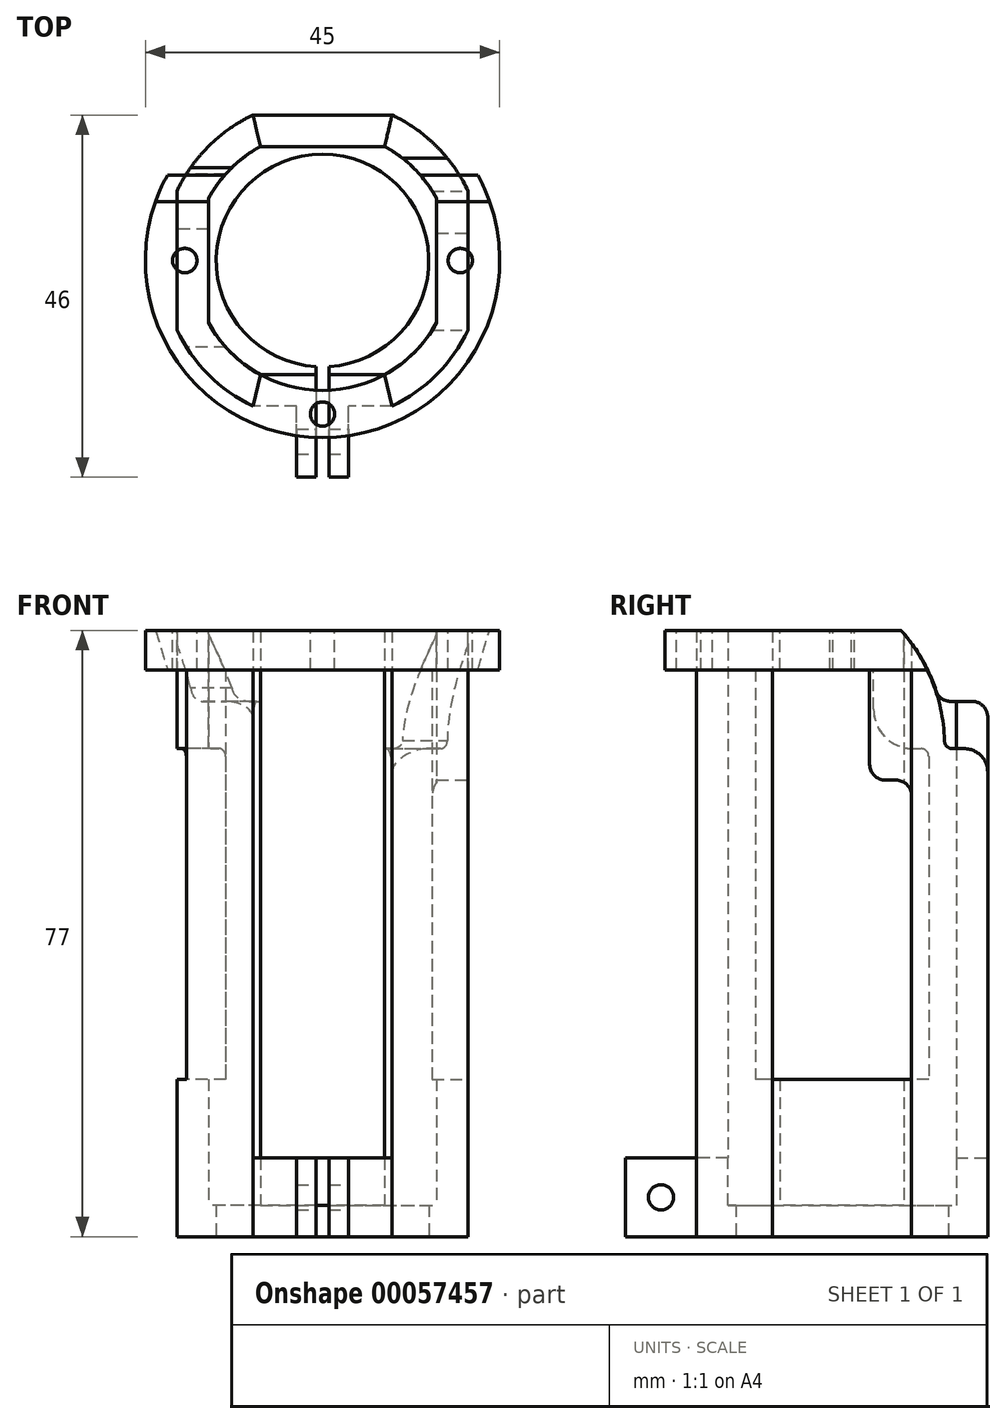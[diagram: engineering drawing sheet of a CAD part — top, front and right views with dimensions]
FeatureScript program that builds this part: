
annotation { "Feature Type Name" : "Feature", "Feature Type Description" : "" }
export const myFeature = defineFeature(function(context is Context, id is Id, definition is map)
    precondition{}
    {
        {
            var Q0;
            Q0=qCreatedBy(makeId("Top.planeOp"),FACE);
            var sketch = newSketch(context, id + "F0", { "sketchPlane" : qUnion([Q0])});
            skArc(sketch, "E0", {"start": v(-7.87, 14.5) * mm, "mid": v(-11.67, 11.67) * mm, "end": v(-14.5, 7.87) * mm});
            skArc(sketch, "E1", {"start": v(-8.83, 18.5) * mm, "mid": v(-14.5, 14.5) * mm, "end": v(-18.5, 8.83) * mm});
            skLineSegment(sketch, "E2.trimOffspring", {"start": v(-7.87, 14.5) * mm, "end": v(7.87, 14.5) * mm});
            skLineSegment(sketch, "E3.1.0", {"start": v(-14.5, -7.87) * mm, "end": v(-14.5, 7.87) * mm});
            skLineSegment(sketch, "E3.2.0", {"start": v(7.87, -14.5) * mm, "end": v(-7.87, -14.5) * mm});
            skLineSegment(sketch, "E3.3.0", {"start": v(14.5, 7.87) * mm, "end": v(14.5, -7.87) * mm});
            skArc(sketch, "E4.trimOffspring", {"start": v(-14.5, -7.87) * mm, "mid": v(-11.67, -11.67) * mm, "end": v(-7.87, -14.5) * mm});
            skArc(sketch, "E5.trimOffspring", {"start": v(14.5, 7.87) * mm, "mid": v(11.67, 11.67) * mm, "end": v(7.87, 14.5) * mm});
            skArc(sketch, "E6.trimOffspring", {"start": v(7.87, -14.5) * mm, "mid": v(11.67, -11.67) * mm, "end": v(14.5, -7.87) * mm});
            skLineSegment(sketch, "E7.0", {"start": v(-8.83, 18.5) * mm, "end": v(8.83, 18.5) * mm});
            skLineSegment(sketch, "E8.1.0", {"start": v(-18.5, -8.83) * mm, "end": v(-18.5, 8.83) * mm});
            skLineSegment(sketch, "E8.2.0", {"start": v(8.83, -18.5) * mm, "end": v(-8.83, -18.5) * mm});
            skLineSegment(sketch, "E8.3.0", {"start": v(18.5, 8.83) * mm, "end": v(18.5, -8.83) * mm});
            skArc(sketch, "E9.trimOffspring", {"start": v(8.83, -18.5) * mm, "mid": v(14.5, -14.5) * mm, "end": v(18.5, -8.83) * mm});
            skArc(sketch, "E10.trimOffspring", {"start": v(18.5, 8.83) * mm, "mid": v(14.5, 14.5) * mm, "end": v(8.83, 18.5) * mm});
            skArc(sketch, "E11.trimOffspring", {"start": v(-18.5, -8.83) * mm, "mid": v(-14.5, -14.5) * mm, "end": v(-8.83, -18.5) * mm});
            skSolve(sketch);
        }
        {
            var Q0;
            Q0 = qSketchRegion(id + "F0", true);
            extrude(context, id + "F1", {"entities" : qUnion([Q0]), "depth" : 10 * mm});
        }
        {
            var Q0;
            Q0=makeQuery(id+"F17.boolean.opBoolean","MERGE",FACE,{"derivedFrom":[makeQuery(id+"F1.opExtrude","CAP_FACE",FACE,{"disambiguationData":[OSD([sQuery(id+"F0.wireOp",EDGE,"E0"),sQuery(id+"F0.wireOp",EDGE,"E1"),sQuery(id+"F0.wireOp",EDGE,"E2.trimOffspring"),sQuery(id+"F0.wireOp",EDGE,"E3.1.0"),sQuery(id+"F0.wireOp",EDGE,"E3.2.0"),sQuery(id+"F0.wireOp",EDGE,"E3.3.0"),sQuery(id+"F0.wireOp",EDGE,"E4.trimOffspring"),sQuery(id+"F0.wireOp",EDGE,"E5.trimOffspring"),sQuery(id+"F0.wireOp",EDGE,"E6.trimOffspring"),sQuery(id+"F0.wireOp",EDGE,"E7.0"),sQuery(id+"F0.wireOp",EDGE,"E8.1.0"),sQuery(id+"F0.wireOp",EDGE,"E8.2.0"),sQuery(id+"F0.wireOp",EDGE,"E8.3.0"),sQuery(id+"F0.wireOp",EDGE,"E9.trimOffspring"),sQuery(id+"F0.wireOp",EDGE,"E10.trimOffspring"),sQuery(id+"F0.wireOp",EDGE,"E11.trimOffspring")])],"isStart":false}),makeQuery(id+"F17.opExtrude","SWEPT_FACE",FACE,{"disambiguationData":[OSD([sQuery(id+"F16.wireOp",EDGE,"E91.top")])]}),makeQuery(id+"F17.opExtrude","SWEPT_FACE",FACE,{"disambiguationData":[OSD([sQuery(id+"F16.wireOp",EDGE,"38b2654b-14ed-417b-8ce9-eae6a770c8082.MirrorCS")])]})]});
            var sketch = newSketch(context, id + "F2", { "sketchPlane" : qUnion([Q0])});
            skArc(sketch, "E12", {"start": v(8.83, -18.5) * mm, "mid": v(14.5, -14.5) * mm, "end": v(18.5, -8.83) * mm});
            skArc(sketch, "E13", {"start": v(8.83, 18.5) * mm, "mid": v(14.5, 14.5) * mm, "end": v(18.5, 8.83) * mm});
            skArc(sketch, "E14", {"start": v(14.5, 7.87) * mm, "mid": v(11.67, 11.67) * mm, "end": v(7.87, 14.5) * mm});
            skArc(sketch, "E15", {"start": v(14.5, -7.87) * mm, "mid": v(11.67, -11.67) * mm, "end": v(7.87, -14.5) * mm});
            skLineSegment(sketch, "E16", {"start": v(14.5, 7.87) * mm, "end": v(14.5, -7.87) * mm});
            skLineSegment(sketch, "E17", {"start": v(18.5, -8.83) * mm, "end": v(18.5, 8.83) * mm});
            skArc(sketch, "E18.MirrorCS", {"start": v(-8.83, -18.5) * mm, "mid": v(-14.5, -14.5) * mm, "end": v(-18.5, -8.83) * mm});
            skArc(sketch, "E19.MirrorCS", {"start": v(-14.5, -7.87) * mm, "mid": v(-11.67, -11.67) * mm, "end": v(-7.87, -14.5) * mm});
            skArc(sketch, "E20.MirrorCS", {"start": v(-8.83, 18.5) * mm, "mid": v(-14.5, 14.5) * mm, "end": v(-18.5, 8.83) * mm});
            skLineSegment(sketch, "E21.MirrorCS", {"start": v(-18.5, -8.83) * mm, "end": v(-18.5, 8.83) * mm});
            skLineSegment(sketch, "E22.MirrorCS", {"start": v(-14.5, 7.87) * mm, "end": v(-14.5, -7.87) * mm});
            skArc(sketch, "E23.MirrorCS", {"start": v(-14.5, 7.87) * mm, "mid": v(-11.67, 11.67) * mm, "end": v(-7.87, 14.5) * mm});
            skLineSegment(sketch, "E24", {"start": v(7.87, 14.5) * mm, "end": v(8.83, 18.5) * mm});
            skPoint(sketch, "E25.orphan", {"position": v(7.01, 19.26) * mm});
            skPoint(sketch, "E26.orphan", {"position": v(5.64, 15.5) * mm});
            skLineSegment(sketch, "E27", {"start": v(7.87, -14.5) * mm, "end": v(8.83, -18.5) * mm});
            skPoint(sketch, "E28.MirrorCS.end.orphan", {"position": v(7.01, -19.26) * mm});
            skPoint(sketch, "E28.MirrorCS.start.orphan", {"position": v(5.64, -15.5) * mm});
            skLineSegment(sketch, "E29", {"start": v(-7.87, 14.5) * mm, "end": v(-8.83, 18.5) * mm});
            skLineSegment(sketch, "E30", {"start": v(-7.87, -14.5) * mm, "end": v(-8.83, -18.5) * mm});
            skPoint(sketch, "E31.MirrorCS.start.orphan", {"position": v(-5.64, -15.5) * mm});
            skPoint(sketch, "E32.orphan", {"position": v(-7.01, -19.26) * mm});
            skPoint(sketch, "E33.orphan", {"position": v(-7.01, 19.26) * mm});
            skPoint(sketch, "E34.orphan", {"position": v(-5.64, 15.5) * mm});
            skSolve(sketch);
        }
        {
            var Q0;
            Q0 = qSketchRegion(id + "F2", true);
            extrude(context, id + "F3", {"entities" : qUnion([Q0]), "operationType" : NewBodyOperationType.ADD, "depth" : 67 * mm});
        }
        {
            var Q0;
            Q0=makeQuery(id+"F3.opExtrude","CAP_FACE",FACE,{"disambiguationData":[OSD([sQuery(id+"F2.wireOp",EDGE,"E18.MirrorCS"),sQuery(id+"F2.wireOp",EDGE,"E19.MirrorCS"),sQuery(id+"F2.wireOp",EDGE,"E20.MirrorCS"),sQuery(id+"F2.wireOp",EDGE,"dc69b4cd-8a5e-4500-a1da-573fba75ecb53.MirrorCS"),sQuery(id+"F2.wireOp",EDGE,"E21.MirrorCS"),sQuery(id+"F2.wireOp",EDGE,"E22.MirrorCS"),sQuery(id+"F2.wireOp",EDGE,"E31.MirrorCS"),sQuery(id+"F2.wireOp",EDGE,"E23.MirrorCS")])],"isStart":false});
            var sketch = newSketch(context, id + "F4", { "sketchPlane" : qUnion([Q0])});
            skArc(sketch, "E35", {"start": v(-14.5, -7.87) * mm, "mid": v(0, -16.5) * mm, "end": v(14.5, -7.87) * mm});
            skArc(sketch, "E36.converted", {"start": v(-12.8, 18.5) * mm, "mid": v(0, -22.5) * mm, "end": v(12.8, 18.5) * mm});
            skLineSegment(sketch, "E37", {"start": v(-12.8, 18.5) * mm, "end": v(12.8, 18.5) * mm});
            skLineSegment(sketch, "E38", {"start": v(-14.5, 7.87) * mm, "end": v(-14.5, -7.87) * mm});
            skLineSegment(sketch, "E39.MirrorCS", {"start": v(14.5, 7.87) * mm, "end": v(14.5, -7.87) * mm});
            skArc(sketch, "E40.trimOffspring", {"start": v(14.5, 7.87) * mm, "mid": v(0, 16.5) * mm, "end": v(-14.5, 7.87) * mm});
            skSolve(sketch);
        }
        {
            var Q0;
            Q0 = qSketchRegion(id + "F4", true);
            extrude(context, id + "F5", {"entities" : qUnion([Q0]), "oppositeDirection" : true, "depth" : 5 * mm});
        }
        {
            var Q0;
            Q0=makeQuery(id+"F5.opExtrude","CAP_FACE",FACE,{"disambiguationData":[OSD([sQuery(id+"F4.wireOp",EDGE,"E35"),sQuery(id+"F4.wireOp",EDGE,"E36.converted"),sQuery(id+"F4.wireOp",EDGE,"E37")])],"isStart":true});
            var sketch = newSketch(context, id + "F6", { "sketchPlane" : qUnion([Q0])});
            skCircle(sketch, "E41", {"center": v(0, -19.5) * mm, "radius": 1.55 * mm});
            skCircle(sketch, "E42", {"center": v(17.5, 0) * mm, "radius": 1.55 * mm});
            skCircle(sketch, "E43", {"center": v(-17.5, 0) * mm, "radius": 1.55 * mm});
            skSolve(sketch);
        }
        {
            var Q0;
            Q0 = qSketchRegion(id + "F6", true);
            extrude(context, id + "F7", {"entities" : qUnion([Q0]), "operationType" : NewBodyOperationType.REMOVE, "oppositeDirection" : true, "depth" : 5 * mm});
        }
        {
            var Q0;
            Q0=makeQuery(id+"F17.boolean.opBoolean","MERGE",FACE,{"derivedFrom":[makeQuery(id+"F1.opExtrude","CAP_FACE",FACE,{"disambiguationData":[OSD([sQuery(id+"F0.wireOp",EDGE,"E0"),sQuery(id+"F0.wireOp",EDGE,"E1"),sQuery(id+"F0.wireOp",EDGE,"E2.trimOffspring"),sQuery(id+"F0.wireOp",EDGE,"E3.1.0"),sQuery(id+"F0.wireOp",EDGE,"E3.2.0"),sQuery(id+"F0.wireOp",EDGE,"E3.3.0"),sQuery(id+"F0.wireOp",EDGE,"E4.trimOffspring"),sQuery(id+"F0.wireOp",EDGE,"E5.trimOffspring"),sQuery(id+"F0.wireOp",EDGE,"E6.trimOffspring"),sQuery(id+"F0.wireOp",EDGE,"E7.0"),sQuery(id+"F0.wireOp",EDGE,"E8.1.0"),sQuery(id+"F0.wireOp",EDGE,"E8.2.0"),sQuery(id+"F0.wireOp",EDGE,"E8.3.0"),sQuery(id+"F0.wireOp",EDGE,"E9.trimOffspring"),sQuery(id+"F0.wireOp",EDGE,"E10.trimOffspring"),sQuery(id+"F0.wireOp",EDGE,"E11.trimOffspring")])],"isStart":true}),makeQuery(id+"F17.opExtrude","SWEPT_FACE",FACE,{"disambiguationData":[OSD([sQuery(id+"F16.wireOp",EDGE,"E91.bottom")])]}),makeQuery(id+"F17.opExtrude","SWEPT_FACE",FACE,{"disambiguationData":[OSD([sQuery(id+"F16.wireOp",EDGE,"38b2654b-14ed-417b-8ce9-eae6a770c8083.MirrorCS")])]})]});
            var sketch = newSketch(context, id + "F8", { "sketchPlane" : qUnion([Q0])});
            skLineSegment(sketch, "E44", {"start": v(-14.5, 7.87) * mm, "end": v(-14.5, -7.87) * mm});
            skLineSegment(sketch, "E45", {"start": v(-7.87, -14.5) * mm, "end": v(7.87, -14.5) * mm});
            skLineSegment(sketch, "E46", {"start": v(-7.87, 14.5) * mm, "end": v(7.87, 14.5) * mm});
            skArc(sketch, "E47", {"start": v(-7.87, 14.5) * mm, "mid": v(-11.67, 11.67) * mm, "end": v(-14.5, 7.87) * mm});
            skArc(sketch, "E48.trimOffspring", {"start": v(-14.5, -7.87) * mm, "mid": v(-11.67, -11.67) * mm, "end": v(-7.87, -14.5) * mm});
            skLineSegment(sketch, "E49", {"start": v(14.5, 7.87) * mm, "end": v(14.5, -7.87) * mm});
            skArc(sketch, "E50.trimOffspring", {"start": v(14.5, 7.87) * mm, "mid": v(11.67, 11.67) * mm, "end": v(7.87, 14.5) * mm});
            skArc(sketch, "E51", {"start": v(7.87, -14.5) * mm, "mid": v(11.67, -11.67) * mm, "end": v(14.5, -7.87) * mm});
            skCircle(sketch, "E52", {"center": v(0, 0) * mm, "radius": 13.5 * mm});
            skSolve(sketch);
        }
        {
            var Q0;
            Q0 = qSketchRegion(id + "F8", true);
            extrude(context, id + "F9", {"entities" : qUnion([Q0]), "operationType" : NewBodyOperationType.ADD, "oppositeDirection" : true, "depth" : 4 * mm});
        }
        {
            var Q0;
            Q0=makeQuery(id+"F3.opExtrude","SWEPT_FACE",FACE,{"disambiguationData":[OSD([sQuery(id+"F2.wireOp",EDGE,"E17")])]});
            var sketch = newSketch(context, id + "F10", { "sketchPlane" : qUnion([Q0])});
            skLineSegment(sketch, "E53", {"start": v(-8.83, 20) * mm, "end": v(-8.83, 72) * mm});
            skLineSegment(sketch, "E54", {"start": v(0, 72) * mm, "end": v(-8.83, 72) * mm});
            skLineSegment(sketch, "E55", {"start": v(-8.83, 20) * mm, "end": v(8.83, 20) * mm});
            skLineSegment(sketch, "E56", {"start": v(8.83, 20) * mm, "end": v(8.83, 56) * mm});
            skLineSegment(sketch, "E57", {"start": v(0, 72) * mm, "end": v(3.5, 72) * mm});
            skLineSegment(sketch, "E58", {"start": v(3.5, 72) * mm, "end": v(3.5, 60) * mm});
            skLineSegment(sketch, "E59", {"start": v(6.83, 58) * mm, "end": v(5.5, 58) * mm});
            skPoint(sketch, "E60.visualSharp", {"position": v(8.83, 58) * mm});
            skArc(sketch, "E60.filletArc", {"start": v(8.83, 56) * mm, "mid": v(8.25, 57.41) * mm, "end": v(6.83, 58) * mm});
            skPoint(sketch, "E61.visualSharp", {"position": v(3.5, 58) * mm});
            skArc(sketch, "E61.filletArc", {"start": v(3.5, 60) * mm, "mid": v(4.09, 58.59) * mm, "end": v(5.5, 58) * mm});
            skLineSegment(sketch, "E62", {"start": v(18.5, 72) * mm, "end": v(18.5, 77) * mm});
            skLineSegment(sketch, "E63", {"start": v(18.5, 72) * mm, "end": v(18.5, 59) * mm});
            skLineSegment(sketch, "E64", {"start": v(18.5, 77) * mm, "end": v(7.5, 77) * mm});
            skArc(sketch, "E65", {"start": v(18.5, 59) * mm, "mid": v(17.62, 61.12) * mm, "end": v(15.5, 62) * mm});
            skLineSegment(sketch, "E66", {"start": v(15.5, 62) * mm, "end": v(14, 62) * mm});
            skArc(sketch, "E67", {"start": v(13, 63) * mm, "mid": v(13.3, 62.3) * mm, "end": v(14, 62) * mm});
            skArc(sketch, "E68", {"start": v(13, 63) * mm, "mid": v(11.48, 70.48) * mm, "end": v(7.5, 77) * mm});
            skSolve(sketch);
        }
        {
            var Q0;
            Q0 = qSketchRegion(id + "F10", true);
            extrude(context, id + "F11", {"entities" : qUnion([Q0]), "operationType" : NewBodyOperationType.REMOVE, "oppositeDirection" : true, "depth" : 20 * mm, "hasSecondDirection" : true, "secondDirectionOppositeDirection" : false, "secondDirectionDepth" : 10 * mm});
        }
        {
            var Q0;
            Q0=makeQuery(id+"F3.opExtrude","SWEPT_FACE",FACE,{"disambiguationData":[OSD([sQuery(id+"F2.wireOp",EDGE,"E21.MirrorCS")])]});
            var sketch = newSketch(context, id + "F12", { "sketchPlane" : qUnion([Q0])});
            skLineSegment(sketch, "E69", {"start": v(0, 72) * mm, "end": v(11, 72) * mm});
            skLineSegment(sketch, "E70", {"start": v(11, 72) * mm, "end": v(11, 20) * mm});
            skLineSegment(sketch, "E71", {"start": v(11, 20) * mm, "end": v(-11, 20) * mm});
            skLineSegment(sketch, "E72", {"start": v(-11, 20) * mm, "end": v(-11, 61) * mm});
            skArc(sketch, "E73", {"start": v(-10, 62) * mm, "mid": v(-10.7, 61.7) * mm, "end": v(-11, 61) * mm});
            skLineSegment(sketch, "E74", {"start": v(-10, 62) * mm, "end": v(-9, 62) * mm});
            skArc(sketch, "E75", {"start": v(-9, 62) * mm, "mid": v(-5.46, 63.46) * mm, "end": v(-4, 67) * mm});
            skLineSegment(sketch, "E76", {"start": v(-4, 67) * mm, "end": v(-4, 72) * mm});
            skLineSegment(sketch, "E77", {"start": v(0, 72) * mm, "end": v(-4, 72) * mm});
            skLineSegment(sketch, "E78", {"start": v(-18.5, 77) * mm, "end": v(-18.5, 66) * mm});
            skArc(sketch, "E79", {"start": v(-16.5, 68) * mm, "mid": v(-17.91, 67.41) * mm, "end": v(-18.5, 66) * mm});
            skLineSegment(sketch, "E80", {"start": v(-16.5, 68) * mm, "end": v(-13.8, 68) * mm});
            skArc(sketch, "E81", {"start": v(-13.8, 68) * mm, "mid": v(-12.5, 68.48) * mm, "end": v(-11.83, 69.68) * mm});
            skPoint(sketch, "E82.start.orphan", {"position": v(0, 77) * mm});
            skLineSegment(sketch, "E83", {"start": v(-18.5, 77) * mm, "end": v(-7.5, 77) * mm});
            skArc(sketch, "E84", {"start": v(-7.5, 77) * mm, "mid": v(-10.02, 73.55) * mm, "end": v(-11.83, 69.68) * mm});
            skSolve(sketch);
        }
        {
            var Q0;
            Q0 = qSketchRegion(id + "F12", true);
            extrude(context, id + "F13", {"entities" : qUnion([Q0]), "operationType" : NewBodyOperationType.REMOVE, "oppositeDirection" : true, "depth" : 20 * mm, "hasSecondDirection" : true, "secondDirectionOppositeDirection" : false, "secondDirectionDepth" : 10 * mm});
        }
        {
            var Q0;
            Q0=makeQuery(id+"F9.boolean.opBoolean","MERGE",FACE,{"derivedFrom":[makeQuery(id+"F1.opExtrude","CAP_FACE",FACE,{"disambiguationData":[OSD([sQuery(id+"F0.wireOp",EDGE,"E0"),sQuery(id+"F0.wireOp",EDGE,"E1"),sQuery(id+"F0.wireOp",EDGE,"E2.trimOffspring"),sQuery(id+"F0.wireOp",EDGE,"E3.1.0"),sQuery(id+"F0.wireOp",EDGE,"E3.2.0"),sQuery(id+"F0.wireOp",EDGE,"E3.3.0"),sQuery(id+"F0.wireOp",EDGE,"E4.trimOffspring"),sQuery(id+"F0.wireOp",EDGE,"E5.trimOffspring"),sQuery(id+"F0.wireOp",EDGE,"E6.trimOffspring"),sQuery(id+"F0.wireOp",EDGE,"E7.0"),sQuery(id+"F0.wireOp",EDGE,"E8.1.0"),sQuery(id+"F0.wireOp",EDGE,"E8.2.0"),sQuery(id+"F0.wireOp",EDGE,"E8.3.0"),sQuery(id+"F0.wireOp",EDGE,"E9.trimOffspring"),sQuery(id+"F0.wireOp",EDGE,"E10.trimOffspring"),sQuery(id+"F0.wireOp",EDGE,"E11.trimOffspring")])],"isStart":true}),makeQuery(id+"F9.opExtrude","CAP_FACE",FACE,{"disambiguationData":[OSD([sQuery(id+"F8.wireOp",EDGE,"E44"),sQuery(id+"F8.wireOp",EDGE,"E45"),sQuery(id+"F8.wireOp",EDGE,"E46"),sQuery(id+"F8.wireOp",EDGE,"E47"),sQuery(id+"F8.wireOp",EDGE,"E48.trimOffspring"),sQuery(id+"F8.wireOp",EDGE,"E49"),sQuery(id+"F8.wireOp",EDGE,"E50.trimOffspring"),sQuery(id+"F8.wireOp",EDGE,"E51"),sQuery(id+"F8.wireOp",EDGE,"E52")])],"isStart":true})]});
            var sketch = newSketch(context, id + "F14", { "sketchPlane" : qUnion([Q0])});
            skLineSegment(sketch, "E85", {"start": v(0, 11.84) * mm, "end": v(0.8, 11.84) * mm});
            skPoint(sketch, "E85.startSnap0", {"position": v(0, 18.5) * mm});
            skLineSegment(sketch, "E86", {"start": v(0.8, 11.84) * mm, "end": v(0.8, 23.3) * mm});
            skLineSegment(sketch, "E87", {"start": v(0.8, 23.3) * mm, "end": v(0, 23.3) * mm});
            skLineSegment(sketch, "E88.MirrorCS", {"start": v(0, 11.84) * mm, "end": v(-0.8, 11.84) * mm});
            skLineSegment(sketch, "E89.MirrorCS", {"start": v(-0.8, 11.84) * mm, "end": v(-0.8, 23.3) * mm});
            skLineSegment(sketch, "E90.MirrorCS", {"start": v(-0.8, 23.3) * mm, "end": v(0, 23.3) * mm});
            skSolve(sketch);
        }
        {
            var Q0;
            Q0 = qSketchRegion(id + "F14", true);
            var Q1;
            Q1=makeQuery(id+"F1.opExtrude","CAP_FACE",FACE,{"disambiguationData":[OSD([sQuery(id+"F0.wireOp",EDGE,"E0"),sQuery(id+"F0.wireOp",EDGE,"E1"),sQuery(id+"F0.wireOp",EDGE,"E2.trimOffspring"),sQuery(id+"F0.wireOp",EDGE,"E3.1.0"),sQuery(id+"F0.wireOp",EDGE,"E3.2.0"),sQuery(id+"F0.wireOp",EDGE,"E3.3.0"),sQuery(id+"F0.wireOp",EDGE,"E4.trimOffspring"),sQuery(id+"F0.wireOp",EDGE,"E5.trimOffspring"),sQuery(id+"F0.wireOp",EDGE,"E6.trimOffspring"),sQuery(id+"F0.wireOp",EDGE,"E7.0"),sQuery(id+"F0.wireOp",EDGE,"E8.1.0"),sQuery(id+"F0.wireOp",EDGE,"E8.2.0"),sQuery(id+"F0.wireOp",EDGE,"E8.3.0"),sQuery(id+"F0.wireOp",EDGE,"E9.trimOffspring"),sQuery(id+"F0.wireOp",EDGE,"E10.trimOffspring"),sQuery(id+"F0.wireOp",EDGE,"E11.trimOffspring")])],"isStart":true});
            extrude(context, id + "F15", {"entities" : qUnion([Q0]), "operationType" : NewBodyOperationType.REMOVE, "oppositeDirection" : true, "endBoundEntityFace" : qUnion([Q1]), "depth" : 10 * mm});
        }
        {
            var Q0;
            {var subQ2=sQuery(id+"F0.wireOp",EDGE,"E9.trimOffspring");var subQ4=sQuery(id+"F0.wireOp",EDGE,"E8.2.0");Q0=makeQuery(id+"F15.boolean.opBoolean","SPLIT",FACE,{"disambiguationData":[TD([makeQuery(id+"F1.opExtrude","SWEPT_FACE",FACE,{"disambiguationData":[OSD([subQ2])]})])],"derivedFrom":makeQuery(id+"F1.opExtrude","SWEPT_FACE",FACE,{"disambiguationData":[OSD([subQ4])]})});}
            var sketch = newSketch(context, id + "F16", { "sketchPlane" : qUnion([Q0])});
            skLineSegment(sketch, "E91.bottom", {"start": v(0.8, 10) * mm, "end": v(3.3, 10) * mm});
            skLineSegment(sketch, "E91.top", {"start": v(0.8, 10) * mm, "end": v(3.3, 10) * mm});
            skLineSegment(sketch, "E91.left", {"start": v(0.8, 10) * mm, "end": v(0.8, 10) * mm});
            skLineSegment(sketch, "E91.right", {"start": v(3.3, 10) * mm, "end": v(3.3, 10) * mm});
            skLineSegment(sketch, "E92", {"start": v(3.3, 10) * mm, "end": v(3.3, 0) * mm});
            skLineSegment(sketch, "E93", {"start": v(3.3, 0) * mm, "end": v(0.8, 0) * mm});
            skLineSegment(sketch, "E94", {"start": v(0.8, 0) * mm, "end": v(0.8, 10) * mm});
            skLineSegment(sketch, "E95.MirrorCS", {"start": v(-0.8, 10) * mm, "end": v(-3.3, 10) * mm});
            skLineSegment(sketch, "E96.MirrorCS", {"start": v(-0.8, 10) * mm, "end": v(-0.8, 10) * mm});
            skLineSegment(sketch, "E97.MirrorCS", {"start": v(-3.3, 0) * mm, "end": v(-0.8, 0) * mm});
            skLineSegment(sketch, "E98.MirrorCS", {"start": v(-3.3, 10) * mm, "end": v(-3.3, 10) * mm});
            skLineSegment(sketch, "E99.MirrorCS", {"start": v(-0.8, 0) * mm, "end": v(-0.8, 10) * mm});
            skLineSegment(sketch, "E100.MirrorCS", {"start": v(-3.3, 10) * mm, "end": v(-3.3, 0) * mm});
            skSolve(sketch);
        }
        {
            var Q0;
            Q0 = qSketchRegion(id + "F16", true);
            extrude(context, id + "F17", {"entities" : qUnion([Q0]), "operationType" : NewBodyOperationType.ADD, "depth" : 9 * mm});
        }
        {
            var Q0;
            Q0=makeQuery(id+"F17.opExtrude","SWEPT_FACE",FACE,{"disambiguationData":[OSD([sQuery(id+"F16.wireOp",EDGE,"E92")])]});
            var sketch = newSketch(context, id + "F18", { "sketchPlane" : qUnion([Q0])});
            skCircle(sketch, "E101", {"center": v(-23, 5) * mm, "radius": 1.6 * mm});
            skPoint(sketch, "E102.orphan", {"position": v(-27.5, 5) * mm});
            skSolve(sketch);
        }
        {
            var Q0;
            Q0 = qSketchRegion(id + "F18", true);
            var Q1;
            Q1=makeQuery(id+"F17.opExtrude","SWEPT_FACE",FACE,{"disambiguationData":[OSD([sQuery(id+"F16.wireOp",EDGE,"E100.MirrorCS")])]});
            extrude(context, id + "F19", {"entities" : qUnion([Q0]), "operationType" : NewBodyOperationType.REMOVE, "endBound" : BoundingType.UP_TO_SURFACE, "oppositeDirection" : true, "endBoundEntityFace" : qUnion([Q1]), "depth" : 25 * mm});
        }
    });
